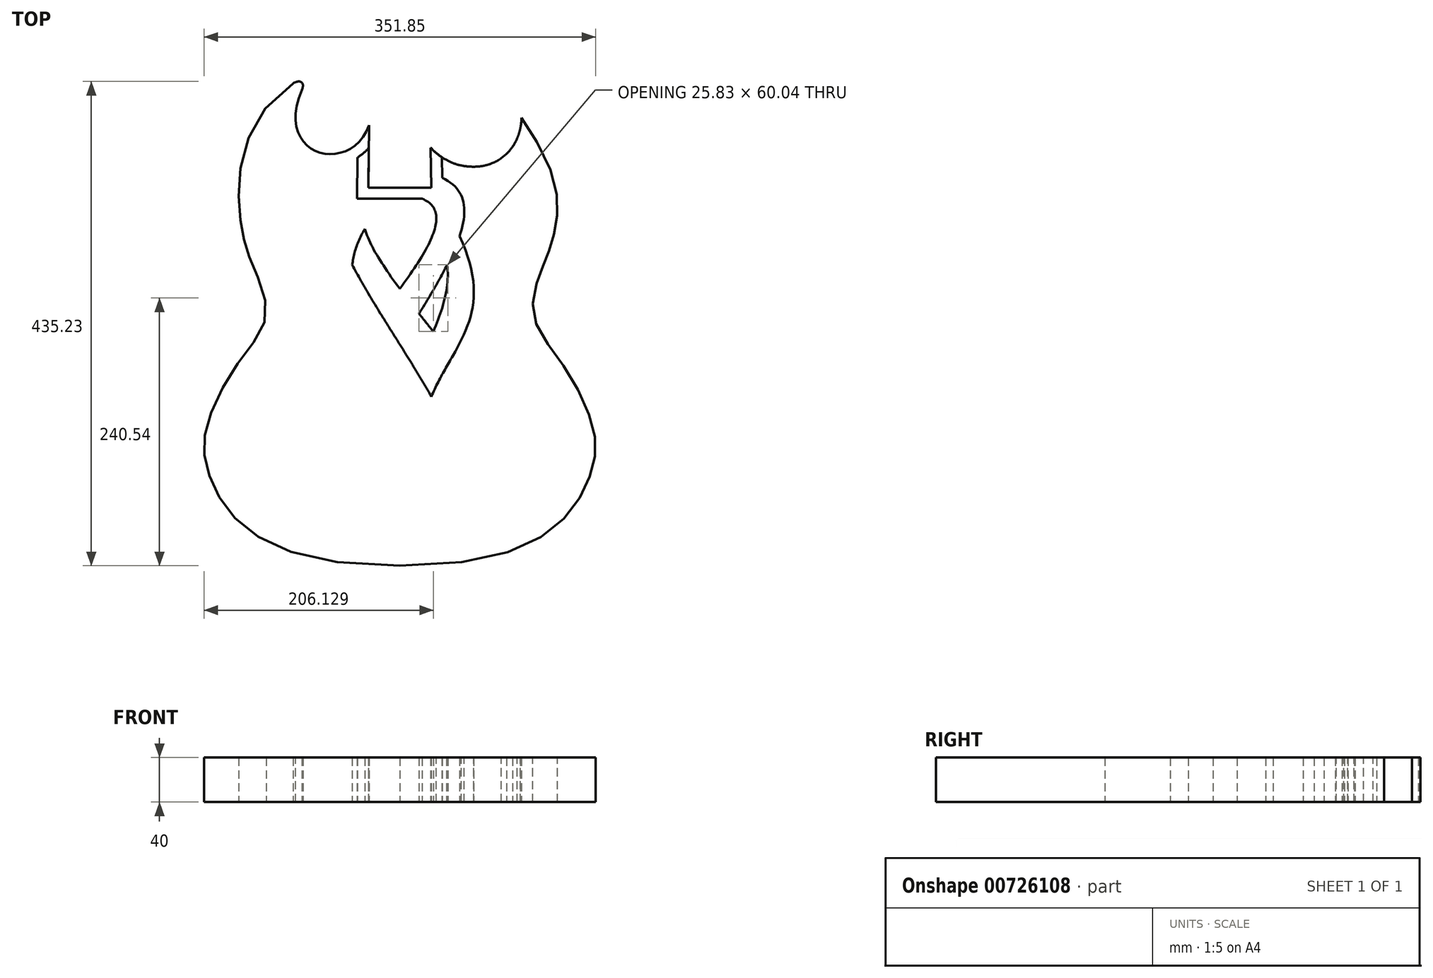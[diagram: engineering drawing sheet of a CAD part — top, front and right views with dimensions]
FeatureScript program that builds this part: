
annotation { "Feature Type Name" : "Feature", "Feature Type Description" : "" }
export const myFeature = defineFeature(function(context is Context, id is Id, definition is map)
    precondition{}
    {
        {
            var Q0;
            Q0=qCreatedBy(makeId("Top.planeOp"),FACE);
            var sketch = newSketch(context, id + "F0", { "sketchPlane" : qUnion([Q0])});
            skFitSpline(sketch, "E0", {"points": [v(-87.85, 227.77) * mm, v(-95.91, 233.44) * mm], "startDerivative": vector(8.11, 19.58) * mm, "endDerivative": vector(-20.32, -12.24) * mm});
            skFitSpline(sketch, "E1", {"points": [v(27.5, 199.76) * mm, v(96.23, 210.57) * mm], "startDerivative": vector(67.79, -132.26) * mm, "endDerivative": vector(-14.51, 133.13) * mm});
            skFitSpline(sketch, "E2", {"points": [v(96.23, 210.57) * mm, v(101.46, 212.07) * mm], "startDerivative": vector(-0.9, 8.06) * mm, "endDerivative": vector(10.94, -9.33) * mm});
            skFitSpline(sketch, "E3", {"points": [v(-87.85, 227.77) * mm, v(-27.55, 196.03) * mm], "startDerivative": vector(-78.42, -180.29) * mm, "endDerivative": vector(50.85, 138.38) * mm});
            skLineSegment(sketch, "E4", {"start": v(-27.25, 219.83) * mm, "end": v(-28.23, 141.16) * mm});
            skLineSegment(sketch, "E5", {"start": v(-28.25, 139.83) * mm, "end": v(28.25, 139.83) * mm});
            skLineSegment(sketch, "E6", {"start": v(28.25, 139.83) * mm, "end": v(27.78, 177.25) * mm});
            skLineSegment(sketch, "E7", {"start": v(27.25, 219.83) * mm, "end": v(-27.25, 219.83) * mm});
            skFitSpline(sketch, "E8", {"points": [v(16.25, 194) * mm, v(19.56, 187.54) * mm, v(27.4, 176.3) * mm, v(41.89, 164.72) * mm, v(55.35, 159.72) * mm, v(66.3, 158.63) * mm, v(74.42, 159.3) * mm, v(82.23, 161.47) * mm, v(89.5, 165.13) * mm, v(95.96, 170.23) * mm, v(101.37, 176.66) * mm, v(105.49, 184.22) * mm, v(108.18, 192.73) * mm, v(109.38, 201.98) * mm, v(109.16, 208.56) * mm, v(108.8, 211.94) * mm, v(16.25, 194) * mm]});
            skPoint(sketch, "E9", {"position": v(0, 219.83) * mm});
            skPoint(sketch, "E10", {"position": v(0, 139.83) * mm});
            skLineSegment(sketch, "E11", {"start": v(-28.23, 141.16) * mm, "end": v(-28.25, 139.83) * mm});
            skFitSpline(sketch, "E12", {"points": [v(-95.91, 233.44) * mm, v(-143.77, 152.08) * mm, v(-141.5, 100.41) * mm, v(-132.75, 71.16) * mm, v(-120, 25.82) * mm, v(-145, -17.28) * mm, v(-173.5, -74.63) * mm, v(-173.5, -110.65) * mm, v(-150, -154.98) * mm, v(0, -199.98) * mm], "startDerivative": vector(-713.64, -449.1) * mm, "endDerivative": vector(1475.8, 0) * mm});
            skFitSpline(sketch, "E13", {"points": [v(-96.9, 231.7) * mm, v(-98.7, 227.54) * mm, v(-101.56, 219.45) * mm, v(-103.63, 208.04) * mm, v(-103.6, 197.4) * mm, v(-101.52, 187.68) * mm, v(-97.56, 179.13) * mm, v(-91.99, 172) * mm, v(-85.17, 166.45) * mm, v(-77.47, 162.57) * mm, v(-69.2, 160.36) * mm, v(-60.63, 159.82) * mm, v(-52.02, 160.96) * mm, v(-43.61, 163.82) * mm, v(-35.7, 168.42) * mm, v(-28.6, 174.76) * mm, v(-22.62, 182.79) * mm, v(-19.56, 189.18) * mm, v(-18.3, 192.63) * mm]});
            skFitSpline(sketch, "E14", {"points": [v(-96.9, 231.7) * mm, v(-98.7, 227.54) * mm, v(-101.56, 219.45) * mm, v(-103.63, 208.04) * mm, v(-103.6, 197.4) * mm, v(-101.52, 187.68) * mm, v(-97.56, 179.13) * mm, v(-91.99, 172) * mm, v(-85.17, 166.45) * mm, v(-77.47, 162.57) * mm, v(-69.2, 160.36) * mm, v(-60.63, 159.82) * mm, v(-52.02, 160.96) * mm, v(-43.61, 163.82) * mm, v(-35.7, 168.42) * mm, v(-28.6, 174.76) * mm, v(-22.62, 182.79) * mm, v(-19.56, 189.18) * mm, v(-18.3, 192.63) * mm]});
            skFitSpline(sketch, "E15", {"points": [v(-90.58, 224.96) * mm, v(-93.94, 222.84) * mm, v(-100.14, 218.35) * mm, v(-108.04, 210.96) * mm, v(-114.67, 203.02) * mm, v(-122, 191.82) * mm, v(-127.27, 179.9) * mm, v(-130.85, 167.78) * mm, v(-132.77, 158.73) * mm, v(-134.03, 149.87) * mm, v(-134.71, 141.37) * mm, v(-134.9, 133.26) * mm, v(-134.66, 125.56) * mm, v(-134.08, 118.28) * mm, v(-133.23, 111.43) * mm, v(-132.46, 106.65) * mm, v(-131.9, 103.6) * mm, v(-131.52, 101.6) * mm, v(-131.04, 99.21) * mm, v(-130.44, 96.47) * mm, v(-129.6, 92.95) * mm, v(-128.45, 88.71) * mm, v(-127.08, 84.44) * mm, v(-125.8, 80.87) * mm, v(-124.92, 78.55) * mm, v(-124.15, 76.62) * mm, v(-123.55, 75.13) * mm, v(-122.9, 73.6) * mm, v(-122, 71.46) * mm, v(-120.8, 68.66) * mm, v(-119.29, 65.12) * mm, v(-117.74, 61.41) * mm, v(-115.7, 56.28) * mm, v(-113.76, 50.9) * mm, v(-112.12, 45.32) * mm, v(-111.09, 41.03) * mm, v(-110.3, 36.65) * mm, v(-109.92, 32.92) * mm, v(-109.8, 29.9) * mm, v(-109.82, 27.6) * mm, v(-109.94, 25.68) * mm, v(-110.1, 24.14) * mm, v(-110.3, 22.61) * mm, v(-110.62, 20.73) * mm, v(-111.3, 17.79) * mm, v(-112.39, 14.24) * mm, v(-114.04, 10.2) * mm, v(-116.6, 5.05) * mm, v(-120.33, -0.98) * mm, v(-125.3, -7.84) * mm, v(-129.6, -13.43) * mm, v(-133.04, -17.92) * mm, v(-135.58, -21.32) * mm, v(-138.04, -24.77) * mm, v(-140.48, -28.33) * mm, v(-142.86, -32) * mm, v(-145.97, -36.98) * mm, v(-149.67, -43.36) * mm, v(-153.74, -51.11) * mm, v(-157.34, -58.8) * mm, v(-159.9, -65.04) * mm, v(-161.62, -69.83) * mm, v(-162.74, -73.3) * mm, v(-163.7, -76.64) * mm, v(-164.46, -79.8) * mm, v(-165.05, -82.82) * mm, v(-165.63, -86.68) * mm, v(-165.97, -91.27) * mm, v(-165.82, -96.62) * mm, v(-165.27, -101.13) * mm, v(-164.57, -104.88) * mm, v(-164.02, -107.29) * mm, v(-163.51, -109.27) * mm, v(-162.97, -111.27) * mm, v(-162.21, -113.8) * mm, v(-161.17, -116.88) * mm, v(-159.61, -121.03) * mm, v(-157.32, -126.28) * mm, v(-154, -132.6) * mm, v(-150.06, -138.87) * mm, v(-146.23, -144) * mm, v(-142.83, -148) * mm, v(-139.2, -151.95) * mm, v(-134.19, -156.7) * mm, v(-127.3, -162.13) * mm, v(-116.73, -168.96) * mm, v(-100.5, -176.62) * mm, v(-74.97, -183.93) * mm, v(-42.3, -188.77) * mm, v(-15.1, -189.96) * mm, v(0, -189.96) * mm]});
            skFitSpline(sketch, "E16", {"points": [v(16.25, 194) * mm, v(19.56, 187.54) * mm, v(27.4, 176.3) * mm, v(41.89, 164.72) * mm, v(55.35, 159.72) * mm, v(66.3, 158.63) * mm, v(74.42, 159.3) * mm, v(82.23, 161.47) * mm, v(89.5, 165.13) * mm, v(95.96, 170.23) * mm, v(101.37, 176.66) * mm, v(105.49, 184.22) * mm, v(108.18, 192.73) * mm, v(109.38, 201.98) * mm, v(109.16, 208.56) * mm, v(108.8, 211.94) * mm]});
            skLineSegment(sketch, "E17", {"start": v(27.78, 177.25) * mm, "end": v(27.25, 219.83) * mm});
            skFitSpline(sketch, "E18", {"points": [v(101.46, 212.07) * mm, v(132.9, 161.94) * mm, v(141.29, 113.25) * mm, v(134.53, 84.76) * mm, v(125.74, 61.5) * mm, v(120, 25.82) * mm, v(145, -17.28) * mm, v(173.5, -74.63) * mm, v(173.5, -110.65) * mm, v(150, -154.98) * mm, v(0, -199.98) * mm], "startDerivative": vector(151, -125.69) * mm, "endDerivative": vector(-1514.5, 0) * mm});
            skFitSpline(sketch, "E19", {"points": [v(93.52, 205.7) * mm, v(93.62, 205.61) * mm, v(93.82, 205.44) * mm, v(94.07, 205.22) * mm, v(94.28, 205.05) * mm, v(94.43, 204.92) * mm, v(94.58, 204.8) * mm, v(94.7, 204.68) * mm, v(94.8, 204.6) * mm, v(94.87, 204.54) * mm, v(94.92, 204.5) * mm, v(94.96, 204.47) * mm, v(95, 204.44) * mm, v(95.02, 204.42) * mm, v(95.03, 204.4) * mm, v(95.05, 204.4) * mm, v(95.06, 204.39) * mm, v(95.06, 204.38) * mm, v(95.06, 204.38) * mm, v(95.06, 204.38) * mm, v(95.06, 204.38) * mm, v(95.06, 204.38) * mm, v(95.06, 204.38) * mm, v(95.07, 204.38) * mm, v(95.08, 204.37) * mm, v(95.1, 204.34) * mm, v(95.15, 204.3) * mm, v(95.22, 204.23) * mm, v(95.3, 204.15) * mm, v(95.44, 204.02) * mm, v(95.64, 203.8) * mm, v(95.92, 203.5) * mm, v(96.24, 203.15) * mm, v(96.71, 202.61) * mm, v(97.37, 201.83) * mm, v(98.25, 200.73) * mm, v(99.22, 199.5) * mm, v(100.6, 197.66) * mm, v(102.48, 195.07) * mm, v(104.9, 191.56) * mm, v(107.44, 187.72) * mm, v(110.04, 183.62) * mm, v(113.53, 177.87) * mm, v(116.94, 171.85) * mm, v(120.07, 165.82) * mm, v(121.87, 162.1) * mm, v(123.19, 159.2) * mm, v(124.42, 156.35) * mm, v(125.8, 152.88) * mm, v(127.23, 148.86) * mm, v(128.83, 143.68) * mm, v(130.3, 137.53) * mm, v(131.36, 130.6) * mm, v(131.8, 124.04) * mm, v(131.69, 117.81) * mm, v(131.13, 111.82) * mm, v(130.2, 106.06) * mm, v(128.95, 100.51) * mm, v(127.46, 95.15) * mm, v(126.06, 90.84) * mm, v(124.88, 87.46) * mm, v(123.98, 84.98) * mm, v(123.06, 82.5) * mm, v(121.8, 79.2) * mm, v(120.48, 75.82) * mm, v(119.11, 72.28) * mm, v(118.06, 69.52) * mm, v(116.98, 66.64) * mm, v(115.87, 63.61) * mm, v(114.73, 60.38) * mm, v(113.23, 55.84) * mm, v(111.83, 50.96) * mm, v(110.68, 45.81) * mm, v(109.99, 41.83) * mm, v(109.52, 37.72) * mm, v(109.32, 33.5) * mm, v(109.42, 29.91) * mm, v(109.7, 27) * mm, v(110, 24.8) * mm, v(110.43, 22.6) * mm, v(110.95, 20.45) * mm, v(111.56, 18.34) * mm, v(112.5, 15.58) * mm, v(113.85, 12.23) * mm, v(115.72, 8.35) * mm, v(117.8, 4.6) * mm, v(120.78, -0.3) * mm, v(124.83, -6.26) * mm, v(129.1, -12.16) * mm, v(132.54, -16.93) * mm, v(134.68, -19.94) * mm, v(136.37, -22.37) * mm, v(138.05, -24.83) * mm, v(140.13, -27.97) * mm, v(142.59, -31.82) * mm, v(145.8, -37.06) * mm, v(149.63, -43.73) * mm, v(153.87, -51.78) * mm, v(157.61, -59.73) * mm, v(160.24, -66.13) * mm, v(162, -71.02) * mm, v(162.93, -73.96) * mm, v(163.58, -76.23) * mm, v(164.17, -78.44) * mm, v(165.02, -82.16) * mm, v(165.77, -87.13) * mm, v(166.04, -92.75) * mm, v(165.77, -97.37) * mm, v(165.28, -101.13) * mm, v(164.77, -104.03) * mm, v(164.12, -107) * mm, v(163.32, -110.1) * mm, v(162.4, -113.24) * mm, v(161, -117.49) * mm, v(158.89, -122.9) * mm, v(155.76, -129.44) * mm, v(152, -135.97) * mm, v(148.29, -141.33) * mm, v(144.97, -145.54) * mm, v(142.29, -148.65) * mm, v(139.42, -151.7) * mm, v(135.33, -155.65) * mm, v(129.66, -160.42) * mm, v(121.8, -165.83) * mm, v(112.7, -170.87) * mm, v(98.65, -177.04) * mm, v(77.13, -183.53) * mm, v(43.71, -188.7) * mm, v(15.65, -189.98) * mm, v(0, -189.98) * mm]});
            skSolve(sketch);
        }
        {
            var Q0;
            Q0=makeQuery(id+"F0.imprint","IMPRINT",FACE,{"disambiguationData":[TD([[makeQuery(id+"F0.imprint","IMPRINT",EDGE,{"derivedFrom":sQuery(id+"F0.wireOp",EDGE,"E0")}),1.0]])]});
            var sketch = newSketch(context, id + "F1", { "sketchPlane" : qUnion([Q0])});
            skFitSpline(sketch, "E20.0", {"points": [v(-90.58, 224.96) * mm, v(-93.94, 222.84) * mm, v(-100.14, 218.35) * mm, v(-108.04, 210.96) * mm, v(-114.67, 203.02) * mm, v(-122, 191.82) * mm, v(-127.27, 179.9) * mm, v(-130.85, 167.78) * mm, v(-132.77, 158.73) * mm, v(-134.03, 149.87) * mm, v(-134.71, 141.37) * mm, v(-134.9, 133.26) * mm, v(-134.66, 125.56) * mm, v(-134.08, 118.28) * mm, v(-133.23, 111.43) * mm, v(-132.46, 106.65) * mm, v(-131.9, 103.6) * mm, v(-131.52, 101.6) * mm, v(-131.04, 99.21) * mm, v(-130.44, 96.47) * mm, v(-129.6, 92.95) * mm, v(-128.45, 88.71) * mm, v(-127.08, 84.44) * mm, v(-125.8, 80.87) * mm, v(-124.92, 78.55) * mm, v(-124.15, 76.62) * mm, v(-123.55, 75.13) * mm, v(-122.9, 73.6) * mm, v(-122, 71.46) * mm, v(-120.8, 68.66) * mm, v(-119.29, 65.12) * mm, v(-117.74, 61.41) * mm, v(-115.7, 56.28) * mm, v(-113.76, 50.9) * mm, v(-112.12, 45.32) * mm, v(-111.09, 41.03) * mm, v(-110.3, 36.65) * mm, v(-109.92, 32.92) * mm, v(-109.8, 29.9) * mm, v(-109.82, 27.6) * mm, v(-109.94, 25.68) * mm, v(-110.1, 24.14) * mm, v(-110.3, 22.61) * mm, v(-110.62, 20.73) * mm, v(-111.3, 17.79) * mm, v(-112.39, 14.24) * mm, v(-114.04, 10.2) * mm, v(-116.6, 5.05) * mm, v(-120.33, -0.98) * mm, v(-125.3, -7.84) * mm, v(-129.6, -13.43) * mm, v(-133.04, -17.92) * mm, v(-135.58, -21.32) * mm, v(-138.04, -24.77) * mm, v(-140.48, -28.33) * mm, v(-142.86, -32) * mm, v(-145.97, -36.98) * mm, v(-149.67, -43.36) * mm, v(-153.74, -51.11) * mm, v(-157.34, -58.8) * mm, v(-159.9, -65.04) * mm, v(-161.62, -69.83) * mm, v(-162.74, -73.3) * mm, v(-163.7, -76.64) * mm, v(-164.46, -79.8) * mm, v(-165.05, -82.82) * mm, v(-165.63, -86.68) * mm, v(-165.97, -91.27) * mm, v(-165.82, -96.62) * mm, v(-165.27, -101.13) * mm, v(-164.57, -104.88) * mm, v(-164.02, -107.29) * mm, v(-163.51, -109.27) * mm, v(-162.97, -111.27) * mm, v(-162.21, -113.8) * mm, v(-161.17, -116.88) * mm, v(-159.61, -121.03) * mm, v(-157.32, -126.28) * mm, v(-154, -132.6) * mm, v(-150.06, -138.87) * mm, v(-146.23, -144) * mm, v(-142.83, -148) * mm, v(-139.2, -151.95) * mm, v(-134.19, -156.7) * mm, v(-127.3, -162.13) * mm, v(-116.73, -168.96) * mm, v(-100.5, -176.62) * mm, v(-74.97, -183.93) * mm, v(-42.3, -188.77) * mm, v(-15.1, -189.96) * mm, v(0, -189.96) * mm]});
            skFitSpline(sketch, "E21.0", {"points": [v(-96.9, 231.7) * mm, v(-98.7, 227.54) * mm, v(-101.56, 219.45) * mm, v(-103.63, 208.04) * mm, v(-103.6, 197.4) * mm, v(-101.52, 187.68) * mm, v(-97.56, 179.13) * mm, v(-91.99, 172) * mm, v(-85.17, 166.45) * mm, v(-77.47, 162.57) * mm, v(-69.2, 160.36) * mm, v(-60.63, 159.82) * mm, v(-52.02, 160.96) * mm, v(-43.61, 163.82) * mm, v(-35.7, 168.42) * mm, v(-28.6, 174.76) * mm, v(-22.62, 182.79) * mm, v(-19.56, 189.18) * mm, v(-18.3, 192.63) * mm]});
            skLineSegment(sketch, "E22.0", {"start": v(-27.25, 219.83) * mm, "end": v(-28.25, 139.83) * mm});
            skLineSegment(sketch, "E23.0", {"start": v(-28.25, 139.83) * mm, "end": v(28.25, 139.83) * mm});
            skLineSegment(sketch, "E24.0", {"start": v(28.25, 139.83) * mm, "end": v(27.78, 177.25) * mm});
            skLineSegment(sketch, "E25.0", {"start": v(27.78, 177.25) * mm, "end": v(27.25, 219.83) * mm});
            skLineSegment(sketch, "E26.0", {"start": v(27.25, 219.83) * mm, "end": v(-27.25, 219.83) * mm});
            skFitSpline(sketch, "E27.0", {"points": [v(16.25, 194) * mm, v(19.56, 187.54) * mm, v(27.4, 176.3) * mm, v(41.89, 164.72) * mm, v(55.35, 159.72) * mm, v(66.3, 158.63) * mm, v(74.42, 159.3) * mm, v(82.23, 161.47) * mm, v(89.5, 165.13) * mm, v(95.96, 170.23) * mm, v(101.37, 176.66) * mm, v(105.49, 184.22) * mm, v(108.18, 192.73) * mm, v(109.38, 201.98) * mm, v(109.16, 208.56) * mm, v(108.8, 211.94) * mm]});
            skFitSpline(sketch, "E28.0", {"points": [v(93.52, 205.7) * mm, v(93.62, 205.61) * mm, v(93.82, 205.44) * mm, v(94.07, 205.22) * mm, v(94.28, 205.05) * mm, v(94.43, 204.92) * mm, v(94.58, 204.8) * mm, v(94.7, 204.68) * mm, v(94.8, 204.6) * mm, v(94.87, 204.54) * mm, v(94.92, 204.5) * mm, v(94.96, 204.47) * mm, v(95, 204.44) * mm, v(95.02, 204.42) * mm, v(95.03, 204.4) * mm, v(95.05, 204.4) * mm, v(95.06, 204.39) * mm, v(95.06, 204.38) * mm, v(95.06, 204.38) * mm, v(95.06, 204.38) * mm, v(95.06, 204.38) * mm, v(95.06, 204.38) * mm, v(95.06, 204.38) * mm, v(95.07, 204.38) * mm, v(95.08, 204.37) * mm, v(95.1, 204.34) * mm, v(95.15, 204.3) * mm, v(95.22, 204.23) * mm, v(95.3, 204.15) * mm, v(95.44, 204.02) * mm, v(95.64, 203.8) * mm, v(95.92, 203.5) * mm, v(96.24, 203.15) * mm, v(96.71, 202.61) * mm, v(97.37, 201.83) * mm, v(98.25, 200.73) * mm, v(99.22, 199.5) * mm, v(100.6, 197.66) * mm, v(102.48, 195.07) * mm, v(104.9, 191.56) * mm, v(107.44, 187.72) * mm, v(110.04, 183.62) * mm, v(113.53, 177.87) * mm, v(116.94, 171.85) * mm, v(120.07, 165.82) * mm, v(121.87, 162.1) * mm, v(123.19, 159.2) * mm, v(124.42, 156.35) * mm, v(125.8, 152.88) * mm, v(127.23, 148.86) * mm, v(128.83, 143.68) * mm, v(130.3, 137.53) * mm, v(131.36, 130.6) * mm, v(131.8, 124.04) * mm, v(131.69, 117.81) * mm, v(131.13, 111.82) * mm, v(130.2, 106.06) * mm, v(128.95, 100.51) * mm, v(127.46, 95.15) * mm, v(126.06, 90.84) * mm, v(124.88, 87.46) * mm, v(123.98, 84.98) * mm, v(123.06, 82.5) * mm, v(121.8, 79.2) * mm, v(120.48, 75.82) * mm, v(119.11, 72.28) * mm, v(118.06, 69.52) * mm, v(116.98, 66.64) * mm, v(115.87, 63.61) * mm, v(114.73, 60.38) * mm, v(113.23, 55.84) * mm, v(111.83, 50.96) * mm, v(110.68, 45.81) * mm, v(109.99, 41.83) * mm, v(109.52, 37.72) * mm, v(109.32, 33.5) * mm, v(109.42, 29.91) * mm, v(109.7, 27) * mm, v(110, 24.8) * mm, v(110.43, 22.6) * mm, v(110.95, 20.45) * mm, v(111.56, 18.34) * mm, v(112.5, 15.58) * mm, v(113.85, 12.23) * mm, v(115.72, 8.35) * mm, v(117.8, 4.6) * mm, v(120.78, -0.3) * mm, v(124.83, -6.26) * mm, v(129.1, -12.16) * mm, v(132.54, -16.93) * mm, v(134.68, -19.94) * mm, v(136.37, -22.37) * mm, v(138.05, -24.83) * mm, v(140.13, -27.97) * mm, v(142.59, -31.82) * mm, v(145.8, -37.06) * mm, v(149.63, -43.73) * mm, v(153.87, -51.78) * mm, v(157.61, -59.73) * mm, v(160.24, -66.13) * mm, v(162, -71.02) * mm, v(162.93, -73.96) * mm, v(163.58, -76.23) * mm, v(164.17, -78.44) * mm, v(165.02, -82.16) * mm, v(165.77, -87.13) * mm, v(166.04, -92.75) * mm, v(165.77, -97.37) * mm, v(165.28, -101.13) * mm, v(164.77, -104.03) * mm, v(164.12, -107) * mm, v(163.32, -110.1) * mm, v(162.4, -113.24) * mm, v(161, -117.49) * mm, v(158.89, -122.9) * mm, v(155.76, -129.44) * mm, v(152, -135.97) * mm, v(148.29, -141.33) * mm, v(144.97, -145.54) * mm, v(142.29, -148.65) * mm, v(139.42, -151.7) * mm, v(135.33, -155.65) * mm, v(129.66, -160.42) * mm, v(121.8, -165.83) * mm, v(112.7, -170.87) * mm, v(98.65, -177.04) * mm, v(77.13, -183.53) * mm, v(43.71, -188.7) * mm, v(15.65, -189.98) * mm, v(0, -189.98) * mm]});
            skPoint(sketch, "E29.0", {"position": v(0, 219.83) * mm});
            skPoint(sketch, "E30.0", {"position": v(0, 139.83) * mm});
            skLineSegment(sketch, "E31", {"start": v(-37.9, 167.29) * mm, "end": v(-38.38, 129.83) * mm});
            skLineSegment(sketch, "E32", {"start": v(-38.38, 129.83) * mm, "end": v(38.38, 129.83) * mm});
            skLineSegment(sketch, "E33", {"start": v(38.38, 129.83) * mm, "end": v(37.9, 168.36) * mm});
            skFitSpline(sketch, "E34", {"points": [v(-38.14, 148.56) * mm, v(56.66, -186.49) * mm], "startDerivative": vector(-264.2, -119.39) * mm, "endDerivative": vector(-161.54, -307.94) * mm});
            skFitSpline(sketch, "E35", {"points": [v(111.27, -171.38) * mm, v(-19.98, 129.83) * mm], "startDerivative": vector(219.09, 189.85) * mm, "endDerivative": vector(223.85, 87.47) * mm});
            skFitSpline(sketch, "E36.MirrorCS", {"points": [v(-111.27, -171.38) * mm, v(19.98, 129.83) * mm], "startDerivative": vector(-219.09, 189.85) * mm, "endDerivative": vector(-223.85, 87.47) * mm});
            skFitSpline(sketch, "E37.MirrorCS", {"points": [v(38.14, 148.56) * mm, v(-56.66, -186.49) * mm], "startDerivative": vector(264.2, -119.39) * mm, "endDerivative": vector(161.54, -307.94) * mm});
            skFitSpline(sketch, "E38", {"points": [v(-34.32, 129.83) * mm, v(-52.47, -187.02) * mm], "startDerivative": vector(-311.4, -464.2) * mm, "endDerivative": vector(-312.5, -541.12) * mm});
            skFitSpline(sketch, "E39", {"points": [v(-8.59, 129.83) * mm, v(-5.33, -189.93) * mm], "startDerivative": vector(-322.01, -299.19) * mm, "endDerivative": vector(-219.62, -443.99) * mm});
            skFitSpline(sketch, "E40.MirrorCS", {"points": [v(8.59, 129.83) * mm, v(5.33, -189.93) * mm], "startDerivative": vector(322.01, -299.19) * mm, "endDerivative": vector(219.62, -443.99) * mm});
            skFitSpline(sketch, "E41.MirrorCS", {"points": [v(34.32, 129.83) * mm, v(52.47, -187.02) * mm], "startDerivative": vector(311.4, -464.2) * mm, "endDerivative": vector(312.5, -541.12) * mm});
            skFitSpline(sketch, "E42", {"points": [v(-88.9, 169.6) * mm, v(-105.6, -173.9) * mm], "startDerivative": vector(105.6, -368.86) * mm, "endDerivative": vector(178.67, -230.69) * mm});
            skFitSpline(sketch, "E43", {"points": [v(-70.08, 160.8) * mm, v(-61.26, -185.8) * mm], "startDerivative": vector(64.53, -349.22) * mm, "endDerivative": vector(149.01, -206.48) * mm});
            skFitSpline(sketch, "E44.MirrorCS", {"points": [v(70.08, 160.8) * mm, v(61.26, -185.8) * mm], "startDerivative": vector(-64.53, -349.22) * mm, "endDerivative": vector(-149.01, -206.48) * mm});
            skFitSpline(sketch, "E45.MirrorCS", {"points": [v(70.08, 160.8) * mm, v(61.26, -185.8) * mm], "startDerivative": vector(-64.53, -349.22) * mm, "endDerivative": vector(-149.01, -206.48) * mm});
            skFitSpline(sketch, "E46.MirrorCS", {"points": [v(88.9, 169.6) * mm, v(105.6, -173.9) * mm], "startDerivative": vector(-105.6, -368.86) * mm, "endDerivative": vector(-178.67, -230.69) * mm});
            skFitSpline(sketch, "E47.0", {"points": [v(101.46, 212.07) * mm, v(106.85, 207.58) * mm, v(139.45, 160.17) * mm, v(143.82, 114.9) * mm, v(134.95, 84.45) * mm, v(125.4, 61.9) * mm, v(112.85, 22.6) * mm, v(147.15, -16.08) * mm, v(177.54, -73.39) * mm, v(176.03, -111.37) * mm, v(149.95, -168.86) * mm, v(88, -199.98) * mm, v(0, -199.98) * mm]});
            skFitSpline(sketch, "E48.0", {"points": [v(-95.91, 233.44) * mm, v(-128.95, 212.65) * mm, v(-149.03, 155.38) * mm, v(-142.5, 100.5) * mm, v(-134.29, 71.82) * mm, v(-109.55, 22.69) * mm, v(-147.75, -15.62) * mm, v(-177.42, -73.48) * mm, v(-176.06, -111.35) * mm, v(-149.94, -168.87) * mm, v(-88, -199.98) * mm, v(0, -199.98) * mm]});
            skSolve(sketch);
        }
        {
            var Q0;
            Q0=makeQuery(id+"F0.imprint","IMPRINT",FACE,{"disambiguationData":[TD([[makeQuery(id+"F0.imprint","IMPRINT",EDGE,{"derivedFrom":sQuery(id+"F0.wireOp",EDGE,"E0")}),1.0]])]});
            var Q1;
            {var subQ14=sQuery(id+"F1.wireOp",EDGE,"E23.0");Q1=makeQuery(id+"F1.imprint","IMPRINT",FACE,{"disambiguationData":[TD([[makeQuery(id+"F1.imprint","IMPRINT",EDGE,{"derivedFrom":subQ14}),-1.0]])]});}
            var Q2;
            {var subQ0=sQuery(id+"F1.wireOp",EDGE,"E45.MirrorCS");var subQ1=sQuery(id+"F1.wireOp",EDGE,"E27.0");var subQ2=makeQuery(id+"F1.imprint","INTERSECT",VERTEX,{"derivedFrom":[subQ1,subQ0]});Q2=makeQuery(id+"F1.imprint","IMPRINT",FACE,{"disambiguationData":[TD([[makeQuery(id+"F1.imprint","IMPRINT",EDGE,{"disambiguationData":[TD([[subQ2,-1.0]])],"derivedFrom":subQ1}),-1.0]])]});}
            var Q3;
            {var subQ0=sQuery(id+"F1.wireOp",EDGE,"E33");var subQ1=sQuery(id+"F1.wireOp",EDGE,"E32");var subQ2=makeQuery(id+"F1.imprint","INTERSECT",VERTEX,{"derivedFrom":[subQ1,subQ0]});Q3=makeQuery(id+"F1.imprint","IMPRINT",FACE,{"disambiguationData":[TD([[makeQuery(id+"F1.imprint","IMPRINT",EDGE,{"disambiguationData":[TD([[subQ2,1.0]])],"derivedFrom":subQ1}),-1.0]])]});}
            var Q4;
            {var subQ5=sQuery(id+"F1.wireOp",EDGE,"E36.MirrorCS");var subQ7=sQuery(id+"F1.wireOp",EDGE,"E32");var subQ8=makeQuery(id+"F1.imprint","INTERSECT",VERTEX,{"derivedFrom":[subQ7,subQ5]});Q4=makeQuery(id+"F1.imprint","IMPRINT",FACE,{"disambiguationData":[TD([[makeQuery(id+"F1.imprint","IMPRINT",EDGE,{"disambiguationData":[TD([[subQ8,-1.0]])],"derivedFrom":subQ7}),-1.0]])]});}
            var Q5;
            {var subQ0=sQuery(id+"F1.wireOp",EDGE,"E41.MirrorCS");var subQ1=sQuery(id+"F1.wireOp",EDGE,"E35");var subQ2=makeQuery(id+"F1.imprint","INTERSECT",VERTEX,{"derivedFrom":[subQ1,subQ0]});Q5=makeQuery(id+"F1.imprint","IMPRINT",FACE,{"disambiguationData":[TD([[makeQuery(id+"F1.imprint","IMPRINT",EDGE,{"disambiguationData":[TD([[subQ2,-1.0]])],"derivedFrom":subQ1}),-1.0]])]});}
            var Q6;
            {var subQ0=sQuery(id+"F1.wireOp",EDGE,"E37.MirrorCS");var subQ1=sQuery(id+"F1.wireOp",EDGE,"E35");var subQ2=makeQuery(id+"F1.imprint","INTERSECT",VERTEX,{"derivedFrom":[subQ1,subQ0]});Q6=makeQuery(id+"F1.imprint","IMPRINT",FACE,{"disambiguationData":[TD([[makeQuery(id+"F1.imprint","IMPRINT",EDGE,{"disambiguationData":[TD([[subQ2,-1.0]])],"derivedFrom":subQ1}),-1.0]])]});}
            var Q7;
            {var subQ0=sQuery(id+"F1.wireOp",EDGE,"E39");var subQ1=sQuery(id+"F1.wireOp",EDGE,"E34");var subQ2=makeQuery(id+"F1.imprint","INTERSECT",VERTEX,{"derivedFrom":[subQ1,subQ0]});Q7=makeQuery(id+"F1.imprint","IMPRINT",FACE,{"disambiguationData":[TD([[makeQuery(id+"F1.imprint","IMPRINT",EDGE,{"disambiguationData":[TD([[subQ2,-1.0]])],"derivedFrom":subQ1}),1.0]])]});}
            var Q8;
            {var subQ0=sQuery(id+"F1.wireOp",EDGE,"E36.MirrorCS");var subQ1=sQuery(id+"F1.wireOp",EDGE,"E34");var subQ2=makeQuery(id+"F1.imprint","INTERSECT",VERTEX,{"derivedFrom":[subQ1,subQ0]});Q8=makeQuery(id+"F1.imprint","IMPRINT",FACE,{"disambiguationData":[TD([[makeQuery(id+"F1.imprint","IMPRINT",EDGE,{"disambiguationData":[TD([[subQ2,-1.0]])],"derivedFrom":subQ1}),1.0]])]});}
            var Q9;
            {var subQ0=sQuery(id+"F1.wireOp",EDGE,"E37.MirrorCS");var subQ1=sQuery(id+"F1.wireOp",EDGE,"E34");var subQ2=makeQuery(id+"F1.imprint","INTERSECT",VERTEX,{"derivedFrom":[subQ1,subQ0]});Q9=makeQuery(id+"F1.imprint","IMPRINT",FACE,{"disambiguationData":[TD([[makeQuery(id+"F1.imprint","IMPRINT",EDGE,{"disambiguationData":[TD([[subQ2,-1.0]])],"derivedFrom":subQ1}),1.0]])]});}
            var Q10;
            {var subQ1=sQuery(id+"F1.wireOp",EDGE,"E28.0");var subQ4=sQuery(id+"F1.wireOp",EDGE,"E34");var subQ5=makeQuery(id+"F1.imprint","INTERSECT",VERTEX,{"derivedFrom":[subQ1,subQ4]});Q10=makeQuery(id+"F1.imprint","IMPRINT",FACE,{"disambiguationData":[TD([[makeQuery(id+"F1.imprint","IMPRINT",EDGE,{"disambiguationData":[TD([[subQ5,1.0]])],"derivedFrom":subQ1}),-1.0]])]});}
            var Q11;
            {var subQ0=sQuery(id+"F1.wireOp",EDGE,"E41.MirrorCS");var subQ1=sQuery(id+"F1.wireOp",EDGE,"E34");var subQ2=makeQuery(id+"F1.imprint","INTERSECT",VERTEX,{"derivedFrom":[subQ1,subQ0]});Q11=makeQuery(id+"F1.imprint","IMPRINT",FACE,{"disambiguationData":[TD([[makeQuery(id+"F1.imprint","IMPRINT",EDGE,{"disambiguationData":[TD([[subQ2,1.0]])],"derivedFrom":subQ1}),1.0]])]});}
            extrude(context, id + "F2", {"entities" : qUnion([Q0, Q1, Q2, Q3, Q4, Q5, Q6, Q7, Q8, Q9, Q10, Q11]), "depth" : 40 * mm, "offsetDistance" : 25 * mm});
        }
    });
